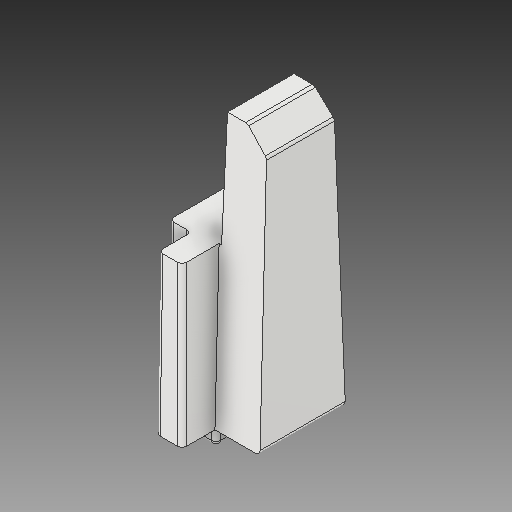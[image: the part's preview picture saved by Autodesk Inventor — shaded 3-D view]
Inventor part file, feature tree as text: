
AUTODESK INVENTOR PART (.ipt)
format: ipt  version: 2019 (Build 230136000, 136)  size: 175,104 bytes
history: native  units: in
note: dims shown in document units (in); Inventor stores cm internally (conversion verified against a paired STEP export)
features: fillet x1
ambient origin geometry x8: Origin, YZ Plane, XZ Plane, XY Plane, X Axis, Y Axis, Z Axis, Center Point
bodies: Solid1 (feature_tree)
feature tree (1):
  fillet  "Fillet4"  [1 undecoded]
note: 1 required parameter value undecoded (feature->parameter linkage not recoverable at this tier; creation-order binding heuristic only, values carry confidence <= 0.55)
